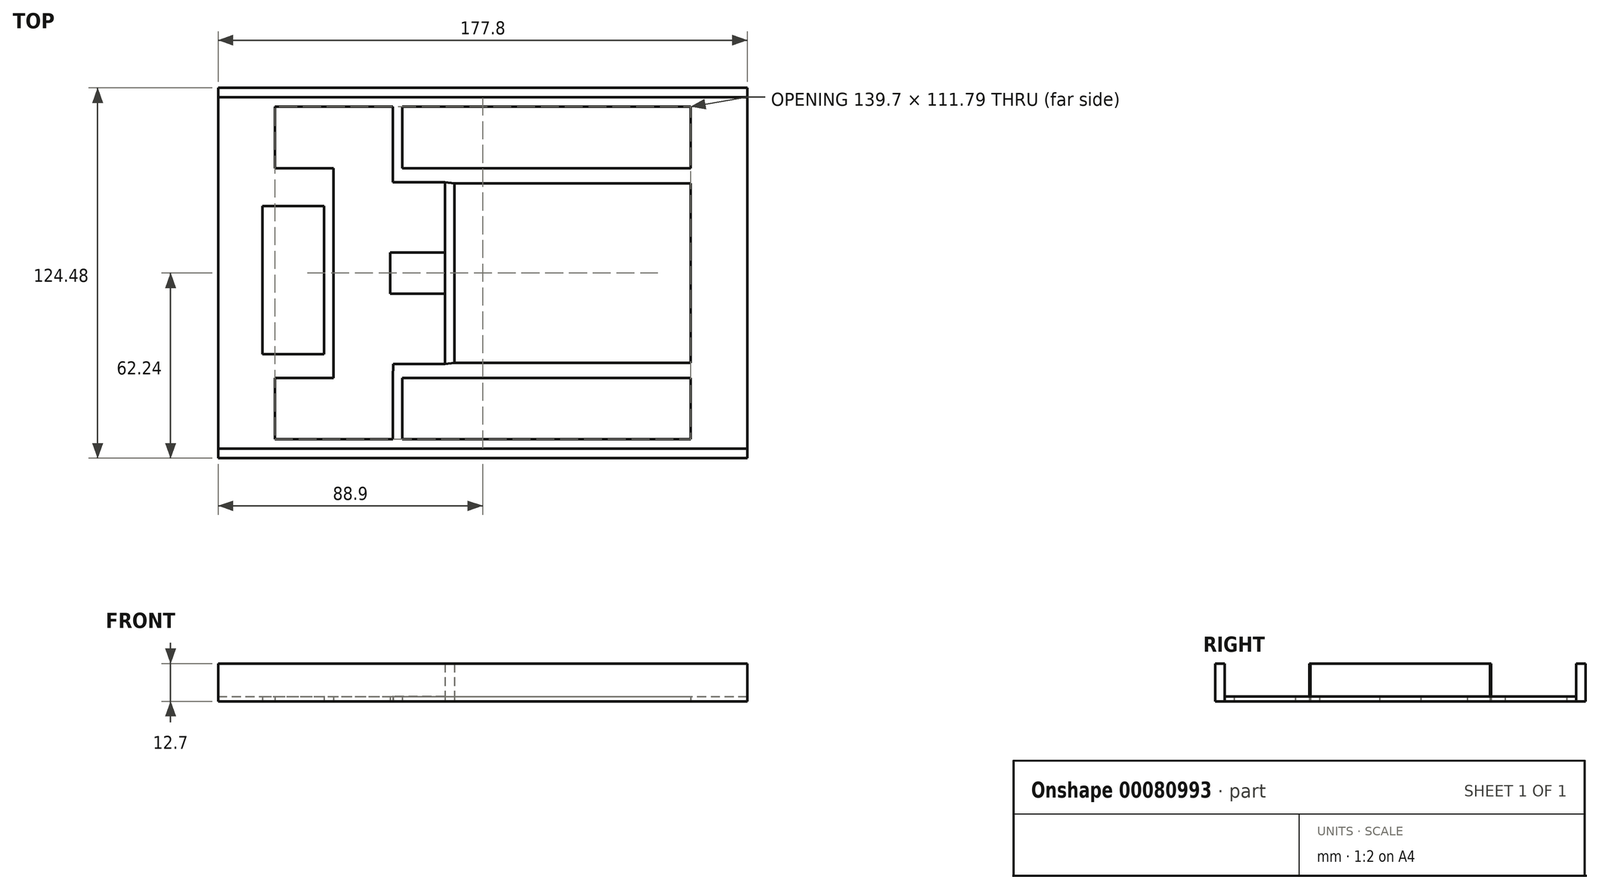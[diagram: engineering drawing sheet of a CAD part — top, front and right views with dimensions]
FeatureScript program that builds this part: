
annotation { "Feature Type Name" : "Feature", "Feature Type Description" : "" }
export const myFeature = defineFeature(function(context is Context, id is Id, definition is map)
    precondition{}
    {
        {
            var Q0;
            Q0=qCreatedBy(makeId("Top.planeOp"),FACE);
            var sketch = newSketch(context, id + "F0", { "sketchPlane" : qUnion([Q0])});
            skLineSegment(sketch, "E0.bottom", {"start": v(-57.15, 63.32) * mm, "end": v(120.65, 63.32) * mm});
            skLineSegment(sketch, "E0.top", {"start": v(-57.15, -61.16) * mm, "end": v(120.65, -61.16) * mm});
            skLineSegment(sketch, "E0.left", {"start": v(-57.15, 63.32) * mm, "end": v(-57.15, -61.16) * mm});
            skLineSegment(sketch, "E0.right", {"start": v(120.65, 63.32) * mm, "end": v(120.65, -61.16) * mm});
            skLineSegment(sketch, "E1.bottom", {"start": v(4.76, -34.16) * mm, "end": v(101.6, -34.16) * mm});
            skLineSegment(sketch, "E1.top", {"start": v(4.76, -54.81) * mm, "end": v(101.6, -54.81) * mm});
            skLineSegment(sketch, "E1.left", {"start": v(4.76, -34.16) * mm, "end": v(4.76, -54.81) * mm});
            skLineSegment(sketch, "E1.right", {"start": v(101.6, -34.16) * mm, "end": v(101.6, -54.81) * mm});
            skLineSegment(sketch, "E2.bottom", {"start": v(4.75, 56.97) * mm, "end": v(101.6, 56.97) * mm});
            skLineSegment(sketch, "E2.top", {"start": v(4.75, 36.32) * mm, "end": v(101.6, 36.32) * mm});
            skLineSegment(sketch, "E2.left", {"start": v(4.75, 56.97) * mm, "end": v(4.75, 36.32) * mm});
            skLineSegment(sketch, "E2.right", {"start": v(101.6, 56.97) * mm, "end": v(101.6, 36.32) * mm});
            skLineSegment(sketch, "E3.bottom", {"start": v(22.22, 31.24) * mm, "end": v(101.6, 31.24) * mm});
            skLineSegment(sketch, "E3.top", {"start": v(22.23, -29.08) * mm, "end": v(101.6, -29.08) * mm});
            skLineSegment(sketch, "E3.left", {"start": v(22.22, 31.24) * mm, "end": v(22.23, -29.08) * mm});
            skLineSegment(sketch, "E3.right", {"start": v(101.6, 31.24) * mm, "end": v(101.6, -29.08) * mm});
            skLineSegment(sketch, "E4.bottom", {"start": v(-38.1, -54.81) * mm, "end": v(1.59, -54.81) * mm});
            skLineSegment(sketch, "E4.left", {"start": v(-38.1, -54.81) * mm, "end": v(-38.1, -34.16) * mm});
            skLineSegment(sketch, "E4.right", {"start": v(1.59, -54.81) * mm, "end": v(1.59, -34.16) * mm});
            skLineSegment(sketch, "E5.bottom", {"start": v(-38.1, 56.97) * mm, "end": v(1.57, 56.97) * mm});
            skLineSegment(sketch, "E5.left", {"start": v(-38.1, 56.97) * mm, "end": v(-38.1, 36.32) * mm});
            skLineSegment(sketch, "E5.right", {"start": v(1.57, 56.97) * mm, "end": v(1.57, 33.15) * mm});
            skLineSegment(sketch, "E6", {"start": v(-18.42, 36.32) * mm, "end": v(-18.41, -34.16) * mm});
            skLineSegment(sketch, "E7", {"start": v(1.57, 33.15) * mm, "end": v(1.57, 31.62) * mm});
            skLineSegment(sketch, "E8", {"start": v(1.57, 31.62) * mm, "end": v(19.05, 31.62) * mm});
            skLineSegment(sketch, "E9", {"start": v(19.05, 31.62) * mm, "end": v(19.05, 8) * mm});
            skLineSegment(sketch, "E10", {"start": v(19.05, -5.84) * mm, "end": v(19.05, -29.46) * mm});
            skLineSegment(sketch, "E11", {"start": v(19.05, -29.46) * mm, "end": v(1.64, -29.46) * mm});
            skLineSegment(sketch, "E12", {"start": v(1.64, -29.46) * mm, "end": v(1.59, -34.16) * mm});
            skLineSegment(sketch, "E13", {"start": v(-38.1, 36.32) * mm, "end": v(-18.42, 36.32) * mm});
            skLineSegment(sketch, "E14", {"start": v(-38.1, -34.16) * mm, "end": v(-18.41, -34.16) * mm});
            skPoint(sketch, "E15.end.orphan", {"position": v(0, 14.95) * mm});
            skLineSegment(sketch, "E16.bottom", {"start": v(19.05, -5.84) * mm, "end": v(0.64, -5.84) * mm});
            skLineSegment(sketch, "E16.top", {"start": v(19.05, 8) * mm, "end": v(0.63, 8) * mm});
            skLineSegment(sketch, "E16.right", {"start": v(0.64, -5.84) * mm, "end": v(0.63, 8) * mm});
            skLineSegment(sketch, "E17.bottom", {"start": v(-42.24, -26.14) * mm, "end": v(-21.59, -26.14) * mm});
            skLineSegment(sketch, "E17.top", {"start": v(-42.24, 23.62) * mm, "end": v(-21.6, 23.62) * mm});
            skLineSegment(sketch, "E17.left", {"start": v(-42.24, -26.14) * mm, "end": v(-42.24, 23.62) * mm});
            skLineSegment(sketch, "E17.right", {"start": v(-21.59, -26.14) * mm, "end": v(-21.6, 23.62) * mm});
            skLineSegment(sketch, "E18", {"start": v(19.05, 31.62) * mm, "end": v(22.22, 31.24) * mm});
            skLineSegment(sketch, "E19", {"start": v(19.05, -29.46) * mm, "end": v(22.23, -29.08) * mm});
            skLineSegment(sketch, "E20", {"start": v(19.05, -5.84) * mm, "end": v(19.05, 8) * mm});
            skLineSegment(sketch, "E21", {"start": v(-38.1, 56.97) * mm, "end": v(-57.15, 56.97) * mm});
            skLineSegment(sketch, "E22", {"start": v(-38.1, -54.81) * mm, "end": v(-57.15, -54.81) * mm});
            skLineSegment(sketch, "E23", {"start": v(101.6, -54.81) * mm, "end": v(120.65, -54.81) * mm});
            skLineSegment(sketch, "E24", {"start": v(101.6, 56.97) * mm, "end": v(120.65, 56.97) * mm});
            skLineSegment(sketch, "E25", {"start": v(1.59, -54.81) * mm, "end": v(4.76, -54.81) * mm});
            skLineSegment(sketch, "E26", {"start": v(1.57, 56.97) * mm, "end": v(4.75, 56.97) * mm});
            skLineSegment(sketch, "E27", {"start": v(-57.15, 60.15) * mm, "end": v(120.65, 60.15) * mm});
            skLineSegment(sketch, "E28", {"start": v(-57.15, -57.99) * mm, "end": v(120.65, -57.99) * mm});
            skSolve(sketch);
        }
        {
            var Q0;
            Q0=makeQuery(id+"F0.imprint","IMPRINT",FACE,{"disambiguationData":[TD([[makeQuery(id+"F0.imprint","IMPRINT",EDGE,{"derivedFrom":sQuery(id+"F0.wireOp",EDGE,"E16.bottom")}),-1.0]])]});
            var Q1;
            Q1=makeQuery(id+"F0.imprint","IMPRINT",FACE,{"disambiguationData":[TD([[makeQuery(id+"F0.imprint","IMPRINT",EDGE,{"derivedFrom":sQuery(id+"F0.wireOp",EDGE,"E1.bottom")}),1.0]])]});
            var Q2;
            Q2=makeQuery(id+"F0.imprint","IMPRINT",FACE,{"disambiguationData":[TD([[makeQuery(id+"F0.imprint","IMPRINT",EDGE,{"derivedFrom":sQuery(id+"F0.wireOp",EDGE,"E4.left")}),1.0]])]});
            var Q3;
            Q3=makeQuery(id+"F0.imprint","IMPRINT",FACE,{"disambiguationData":[TD([[makeQuery(id+"F0.imprint","IMPRINT",EDGE,{"derivedFrom":sQuery(id+"F0.wireOp",EDGE,"E1.top")}),-1.0]])]});
            var Q4;
            Q4=makeQuery(id+"F0.imprint","IMPRINT",FACE,{"disambiguationData":[TD([[makeQuery(id+"F0.imprint","IMPRINT",EDGE,{"derivedFrom":sQuery(id+"F0.wireOp",EDGE,"E2.bottom")}),1.0]])]});
            extrude(context, id + "F1", {"entities" : qUnion([Q0, Q1, Q2, Q3, Q4]), "depth" : 1.59 * mm});
        }
        {
            var Q0;
            Q0=makeQuery(id+"F0.imprint","IMPRINT",FACE,{"disambiguationData":[TD([[makeQuery(id+"F0.imprint","IMPRINT",EDGE,{"derivedFrom":sQuery(id+"F0.wireOp",EDGE,"E3.left")}),-1.0]])]});
            var Q1;
            {var subQ0=sQuery(id+"F0.wireOp",EDGE,"E0.top");Q1=makeQuery(id+"F0.imprint","IMPRINT",FACE,{"disambiguationData":[TD([[makeQuery(id+"F0.imprint","IMPRINT",EDGE,{"derivedFrom":subQ0}),1.0]])]});}
            var Q2;
            {var subQ0=sQuery(id+"F0.wireOp",EDGE,"E0.bottom");Q2=makeQuery(id+"F0.imprint","IMPRINT",FACE,{"disambiguationData":[TD([[makeQuery(id+"F0.imprint","IMPRINT",EDGE,{"derivedFrom":subQ0}),-1.0]])]});}
            extrude(context, id + "F2", {"entities" : qUnion([Q0, Q1, Q2]), "depth" : 12.7 * mm});
        }
    });
